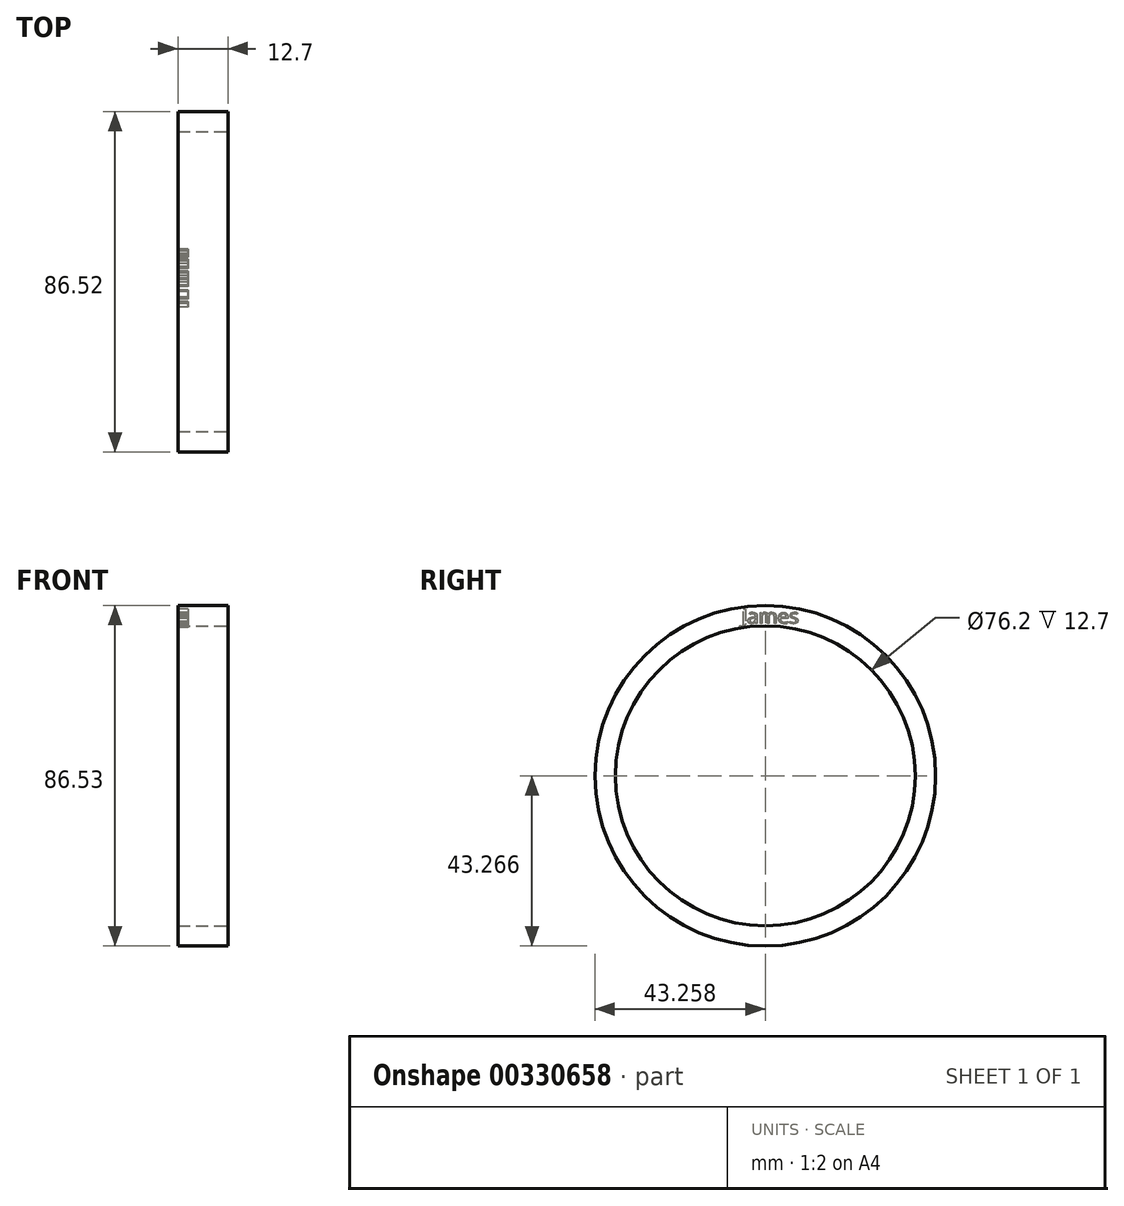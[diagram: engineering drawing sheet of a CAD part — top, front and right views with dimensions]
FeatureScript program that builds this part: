
annotation { "Feature Type Name" : "Feature", "Feature Type Description" : "" }
export const myFeature = defineFeature(function(context is Context, id is Id, definition is map)
    precondition{}
    {
        {
            var Q0;
            Q0=qCreatedBy(makeId("Right.planeOp"),FACE);
            var sketch = newSketch(context, id + "F0", { "sketchPlane" : qUnion([Q0])});
            skCircle(sketch, "E0", {"center": v(-22.07, 15.77) * mm, "radius": 43.26 * mm});
            skSolve(sketch);
        }
        {
            var Q0;
            Q0 = qSketchRegion(id + "F0", true);
            extrude(context, id + "F1", {"entities" : qUnion([Q0]), "depth" : 12.7 * mm});
        }
        {
            var Q0;
            Q0=makeQuery(id+"F1.opExtrude","CAP_FACE",FACE,{"disambiguationData":[OSD([sQuery(id+"F0.wireOp",EDGE,"E0")])],"isStart":false});
            var sketch = newSketch(context, id + "F2", { "sketchPlane" : qUnion([Q0])});
            skCircle(sketch, "E1", {"center": v(-22.07, 15.77) * mm, "radius": 36.91 * mm});
            skSolve(sketch);
        }
        {
            var Q0;
            Q0=sQuery(id+"F2.wireOp",VERTEX,"E1.center");
            var Q1;
            Q1=makeQuery(id+"F1.opExtrude","SWEPT_BODY",BODY,{"disambiguationData":[OSD([sQuery(id+"F0.wireOp",EDGE,"E0")])]});
            hole(context, id + "F3", {"style" : HoleStyle.SIMPLE, "endStyle" : HoleEndStyle.THROUGH, "holeDiameter" : 76.2 * mm, "tappedDepth" : 12.7 * mm, "tapClearance" : 3, "locations" : qUnion([Q0]), "scope" : qUnion([Q1])});
        }
        {
            var Q0;
            Q0=qCreatedBy(makeId("Right.planeOp"),FACE);
            var sketch = newSketch(context, id + "F4", { "sketchPlane" : qUnion([Q0])});
            skText(sketch, "E2", { "text": "James", "fontName": "OpenSans-Regular.ttf"});
            const initialGuessF4  = {"E2": [-0.02805, 0.05445, 1, 0, 0.00373]};
            skSetInitialGuess(sketch, initialGuessF4);
            skSolve(sketch);
        }
        {
            var Q0;
            Q0 = qSketchRegion(id + "F4", true);
            extrude(context, id + "F5", {"entities" : qUnion([Q0]), "operationType" : NewBodyOperationType.REMOVE, "depth" : 2.54 * mm});
        }
    });
